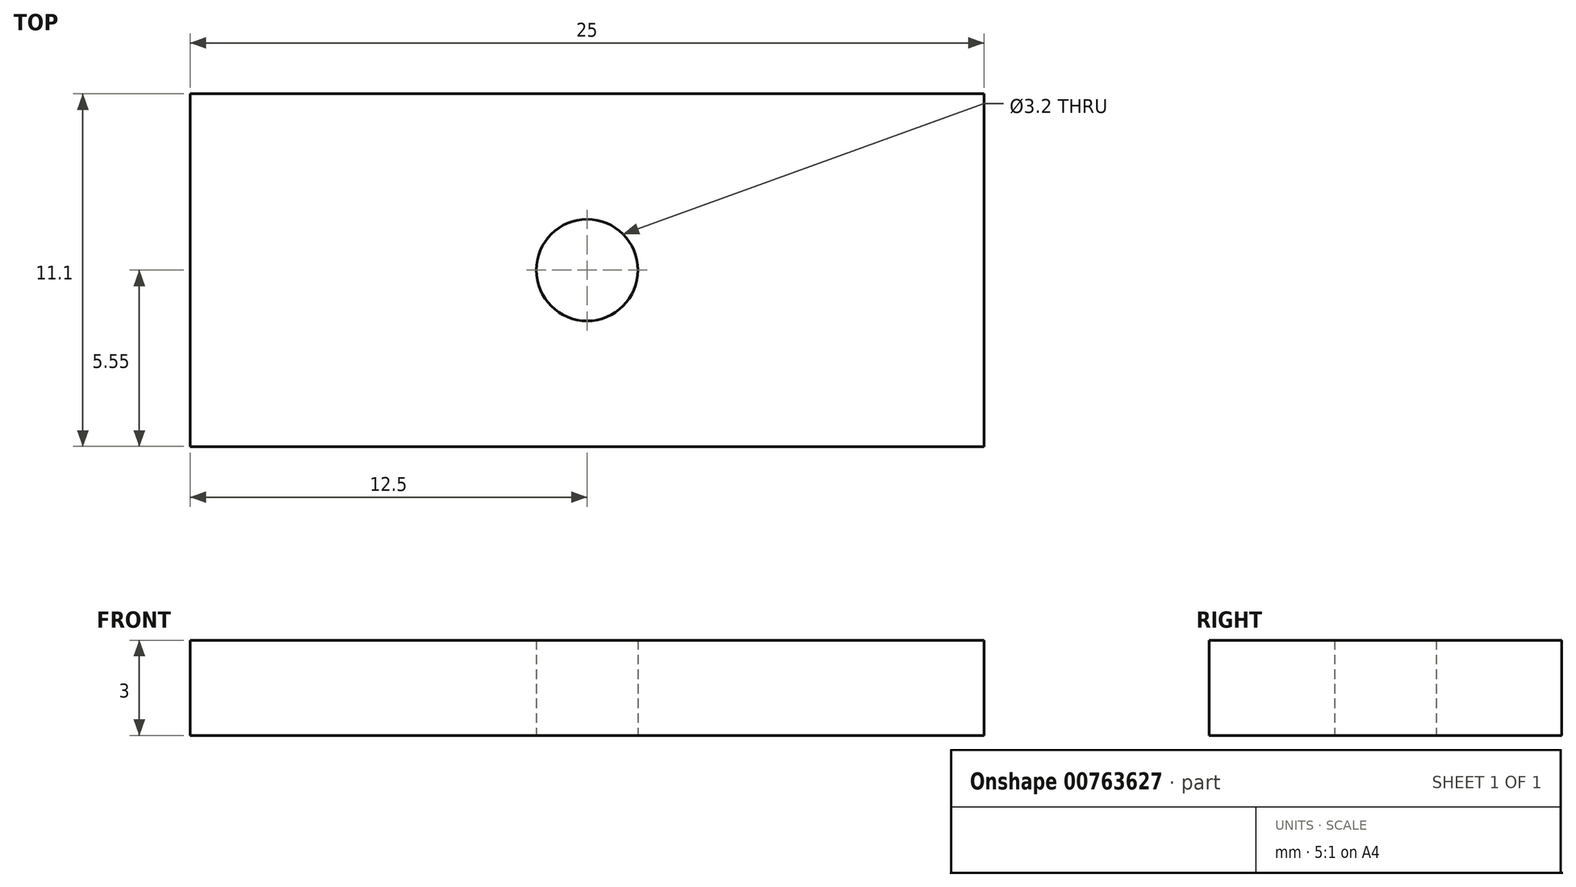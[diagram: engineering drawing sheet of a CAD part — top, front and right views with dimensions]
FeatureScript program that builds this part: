
annotation { "Feature Type Name" : "Feature", "Feature Type Description" : "" }
export const myFeature = defineFeature(function(context is Context, id is Id, definition is map)
    precondition{}
    {
        {
            var Q0;
            Q0=qCreatedBy(makeId("Top.planeOp"),FACE);
            var sketch = newSketch(context, id + "F0", { "sketchPlane" : qUnion([Q0])});
            skLineSegment(sketch, "E0.bottom", {"start": v(12.5, -5.55) * mm, "end": v(-12.5, -5.56) * mm});
            skLineSegment(sketch, "E0.top", {"start": v(12.5, 5.56) * mm, "end": v(-12.5, 5.55) * mm});
            skLineSegment(sketch, "E0.left", {"start": v(12.5, -5.55) * mm, "end": v(12.5, 5.56) * mm});
            skLineSegment(sketch, "E0.right", {"start": v(-12.5, -5.56) * mm, "end": v(-12.5, 5.55) * mm});
            skPoint(sketch, "E0.middle", {"position": v(0, 0) * mm});
            skCircle(sketch, "E1", {"center": v(0, 0) * mm, "radius": 1.6 * mm});
            skSolve(sketch);
        }
        {
            var Q0;
            Q0 = qSketchRegion(id + "F0", true);
            extrude(context, id + "F1", {"entities" : qUnion([Q0]), "depth" : 3 * mm, "offsetDistance" : 25 * mm});
        }
    });
